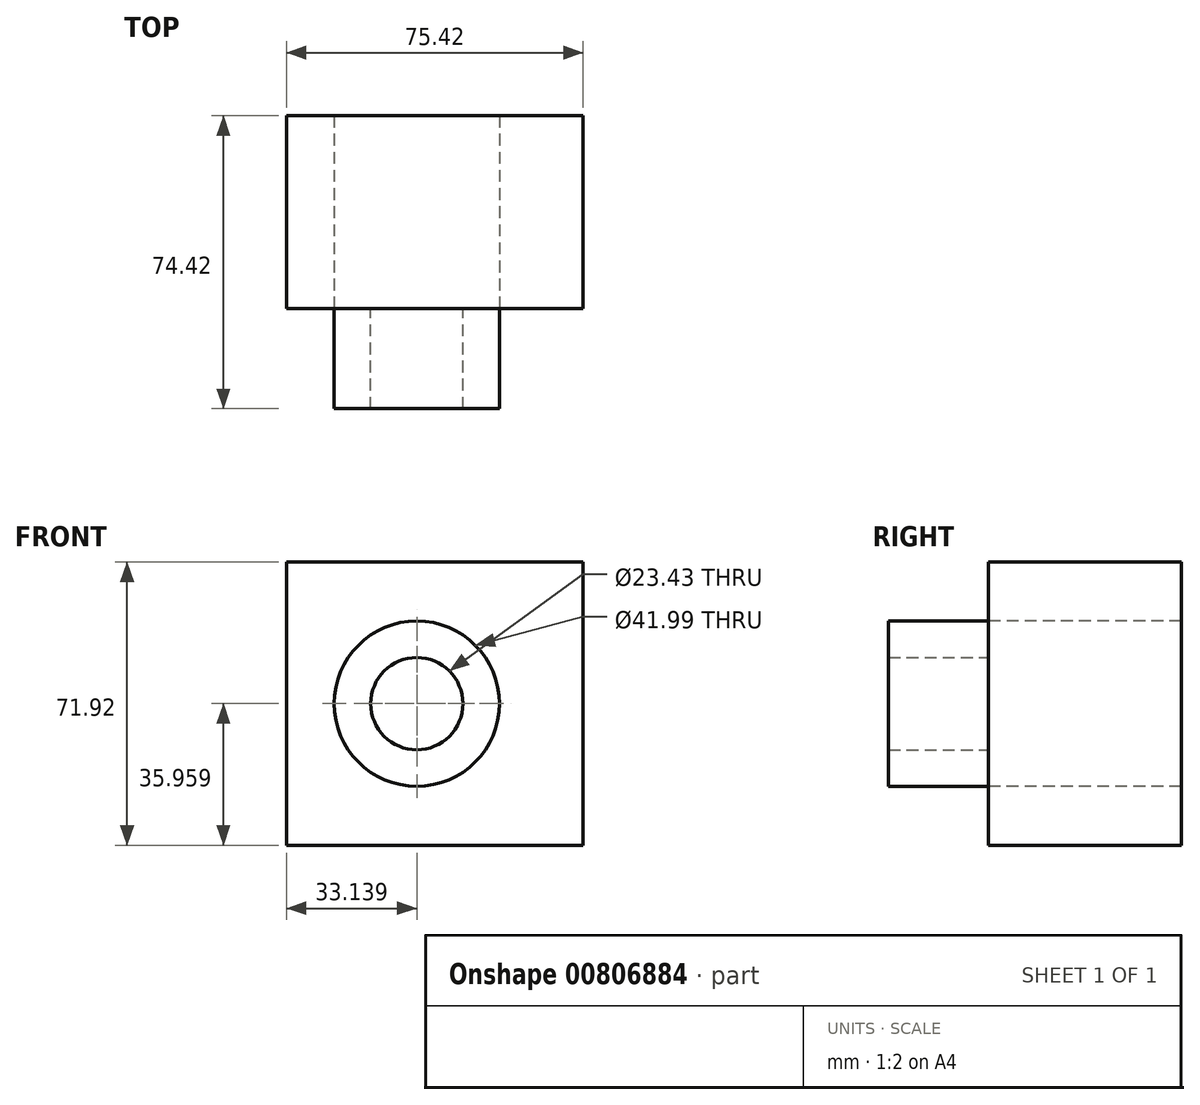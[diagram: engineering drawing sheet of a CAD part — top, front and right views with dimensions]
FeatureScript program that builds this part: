
annotation { "Feature Type Name" : "Feature", "Feature Type Description" : "" }
export const myFeature = defineFeature(function(context is Context, id is Id, definition is map)
    precondition{}
    {
        {
            var Q0;
            Q0=qCreatedBy(makeId("Front.planeOp"),FACE);
            var sketch = newSketch(context, id + "F0", { "sketchPlane" : qUnion([Q0])});
            skLineSegment(sketch, "E0.bottom", {"start": v(-52.42, 17.86) * mm, "end": v(23, 17.86) * mm});
            skLineSegment(sketch, "E0.top", {"start": v(-52.42, -54.06) * mm, "end": v(23, -54.06) * mm});
            skLineSegment(sketch, "E0.left", {"start": v(-52.42, 17.86) * mm, "end": v(-52.42, -54.06) * mm});
            skLineSegment(sketch, "E0.right", {"start": v(23, 17.86) * mm, "end": v(23, -54.06) * mm});
            skCircle(sketch, "E1", {"center": v(-19.28, -18.1) * mm, "radius": 21 * mm});
            skPoint(sketch, "E1.centerSnap0", {"position": v(23, -18.1) * mm});
            skCircle(sketch, "E2", {"center": v(-19.28, -18.1) * mm, "radius": 11.71 * mm});
            skSolve(sketch);
        }
        {
            var Q0;
            Q0 = qSketchRegion(id + "F0", true);
            extrude(context, id + "F1", {"entities" : qUnion([Q0]), "oppositeDirection" : true, "depth" : 49.02 * mm, "offsetDistance" : 25.4 * mm});
        }
        {
            var Q0;
            Q0=makeQuery(id+"F0.imprint","IMPRINT",FACE,{"disambiguationData":[TD([[makeQuery(id+"F0.imprint","IMPRINT",EDGE,{"derivedFrom":sQuery(id+"F0.wireOp",EDGE,"E2")}),1.0]])]});
            extrude(context, id + "F2", {"entities" : qUnion([Q0]), "operationType" : NewBodyOperationType.REMOVE, "endBound" : BoundingType.THROUGH_ALL, "oppositeDirection" : true, "depth" : 25.4 * mm, "offsetDistance" : 25.4 * mm});
        }
        {
            var Q0;
            Q0=makeQuery(id+"F0.imprint","IMPRINT",FACE,{"disambiguationData":[TD([[makeQuery(id+"F0.imprint","IMPRINT",EDGE,{"derivedFrom":sQuery(id+"F0.wireOp",EDGE,"E1")}),1.0]])]});
            extrude(context, id + "F3", {"entities" : qUnion([Q0]), "depth" : 25.4 * mm, "offsetDistance" : 25.4 * mm});
        }
    });
